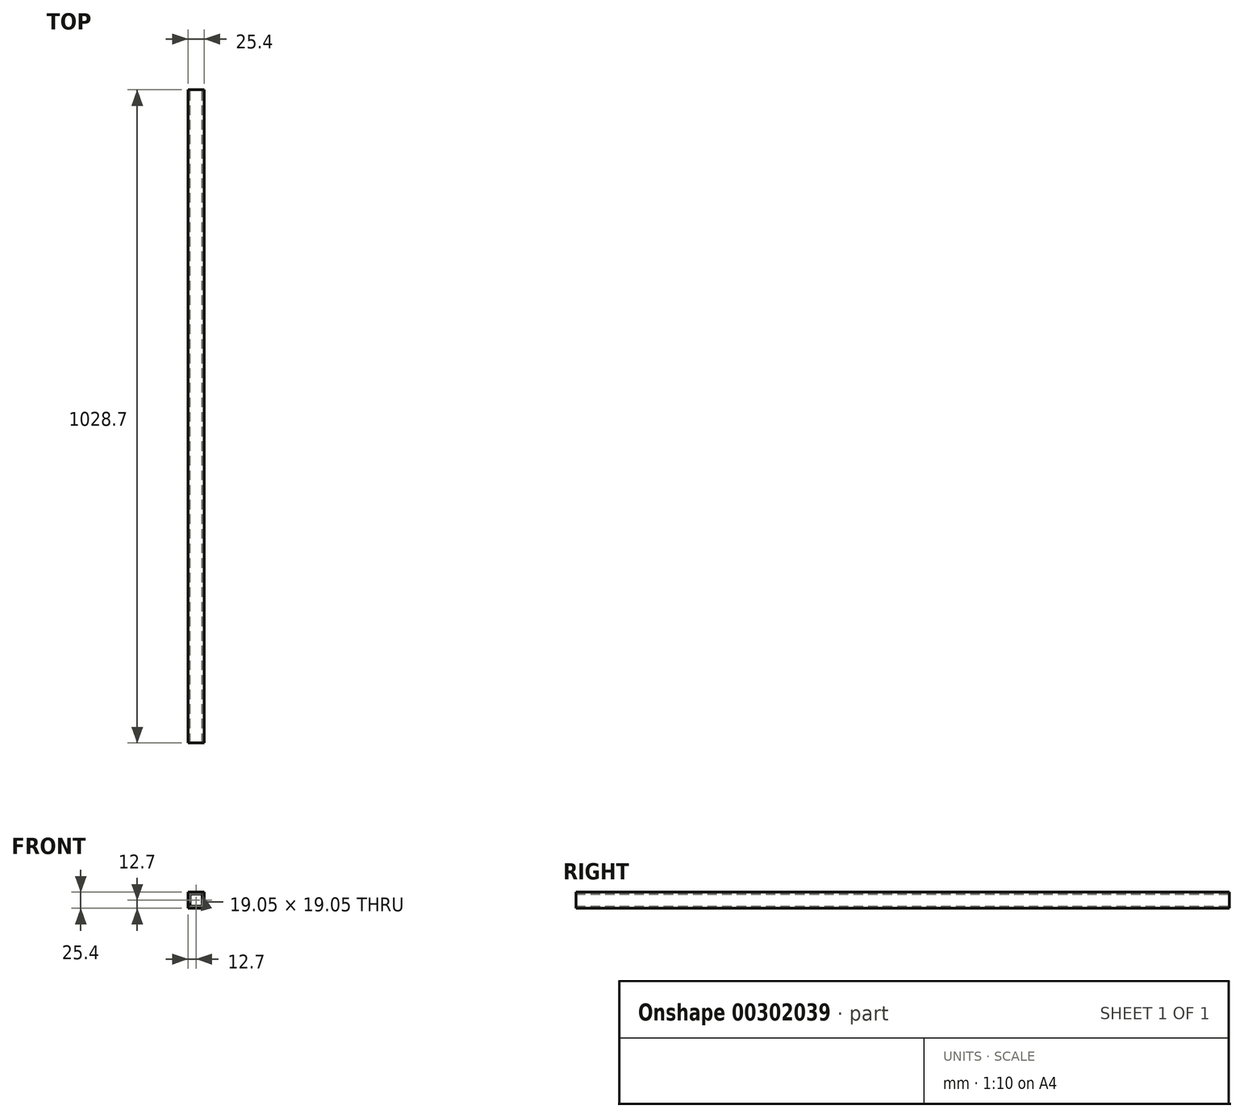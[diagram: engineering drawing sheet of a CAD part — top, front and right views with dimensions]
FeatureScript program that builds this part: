
annotation { "Feature Type Name" : "Feature", "Feature Type Description" : "" }
export const myFeature = defineFeature(function(context is Context, id is Id, definition is map)
    precondition{}
    {
        {
            var Q0;
            Q0=qCreatedBy(makeId("Front.planeOp"),FACE);
            var sketch = newSketch(context, id + "F0", { "sketchPlane" : qUnion([Q0])});
            skLineSegment(sketch, "E0.bottom", {"start": v(12.7, 12.7) * mm, "end": v(-12.7, 12.7) * mm});
            skLineSegment(sketch, "E0.top", {"start": v(12.7, -12.7) * mm, "end": v(-12.7, -12.7) * mm});
            skLineSegment(sketch, "E0.left", {"start": v(12.7, 12.7) * mm, "end": v(12.7, -12.7) * mm});
            skLineSegment(sketch, "E0.right", {"start": v(-12.7, 12.7) * mm, "end": v(-12.7, -12.7) * mm});
            skPoint(sketch, "E0.middle", {"position": v(0, 0) * mm});
            skLineSegment(sketch, "E1.bottom", {"start": v(9.53, 9.52) * mm, "end": v(-9.53, 9.52) * mm});
            skLineSegment(sketch, "E1.top", {"start": v(9.53, -9.53) * mm, "end": v(-9.53, -9.53) * mm});
            skLineSegment(sketch, "E1.left", {"start": v(9.53, 9.53) * mm, "end": v(9.53, -9.53) * mm});
            skLineSegment(sketch, "E1.right", {"start": v(-9.53, 9.53) * mm, "end": v(-9.53, -9.53) * mm});
            skSolve(sketch);
        }
        {
            var Q0;
            Q0 = qSketchRegion(id + "F0", true);
            extrude(context, id + "F1", {"entities" : qUnion([Q0]), "depth" : 1028.7 * mm});
        }
    });
